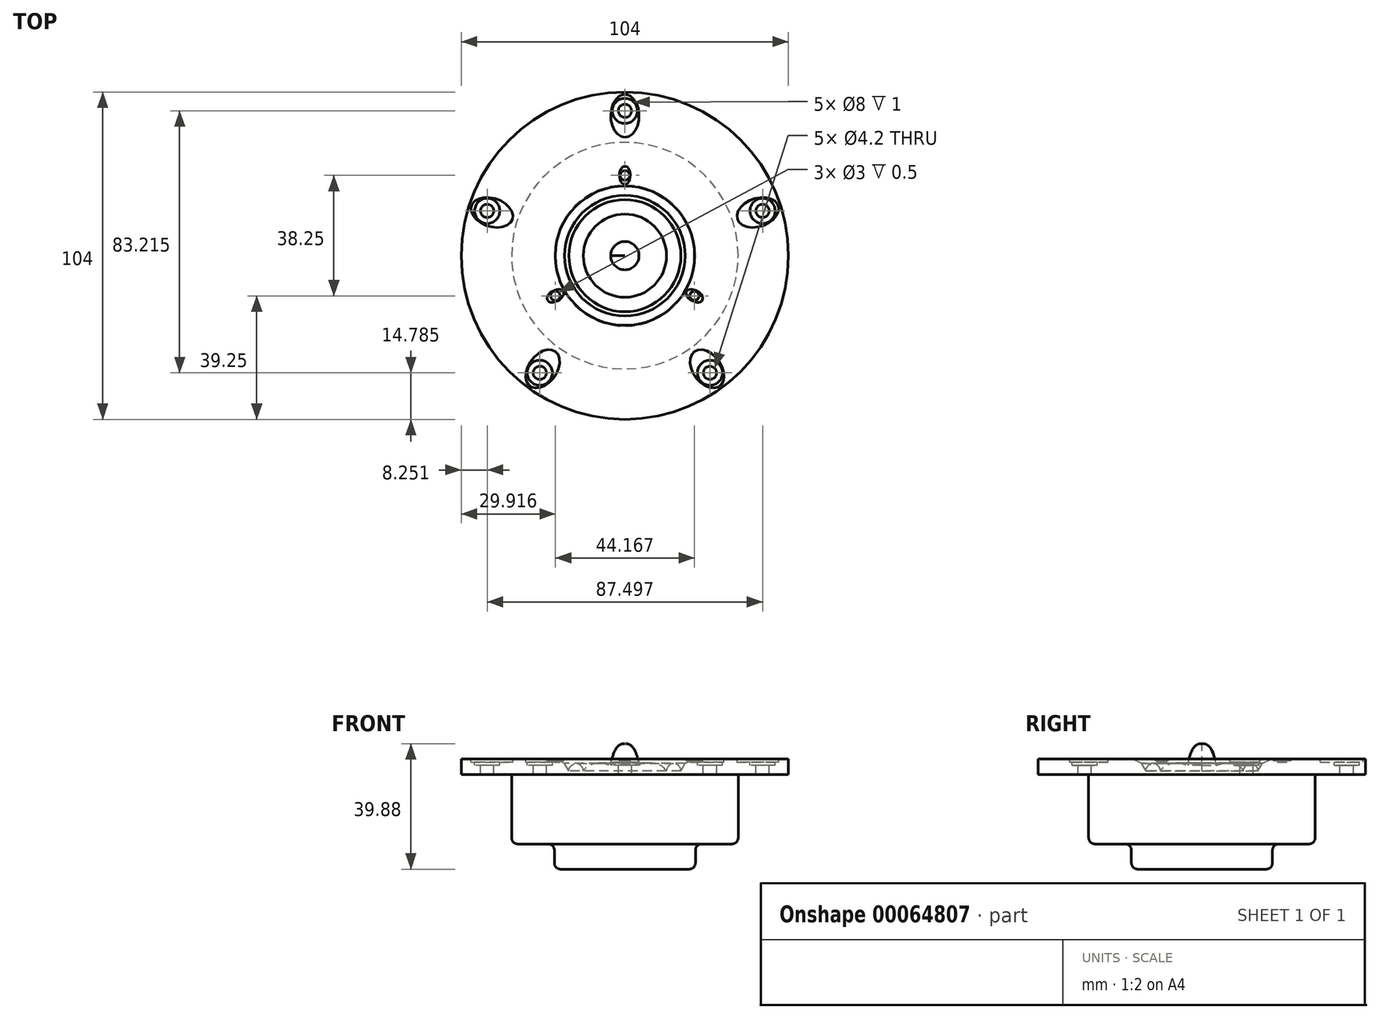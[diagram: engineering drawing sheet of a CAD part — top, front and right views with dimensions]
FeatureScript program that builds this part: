
annotation { "Feature Type Name" : "Feature", "Feature Type Description" : "" }
export const myFeature = defineFeature(function(context is Context, id is Id, definition is map)
    precondition{}
    {
        {
            var Q0;
            Q0=qCreatedBy(makeId("Front.planeOp"),FACE);
            var sketch = newSketch(context, id + "F7", { "sketchPlane" : qUnion([Q0])});
            skLineSegment(sketch, "E0", {"start": v(-52, 16.61) * mm, "end": v(-22.14, 16.61) * mm});
            skLineSegment(sketch, "E1", {"start": v(-52, 16.61) * mm, "end": v(-52, 11.61) * mm});
            skLineSegment(sketch, "E2", {"start": v(-52, 11.61) * mm, "end": v(-36, 11.61) * mm});
            skLineSegment(sketch, "E3", {"start": v(-36, 11.61) * mm, "end": v(-36, -8.39) * mm});
            skLineSegment(sketch, "E4", {"start": v(-20.42, -18.39) * mm, "end": v(0, -18.39) * mm});
            skLineSegment(sketch, "E5", {"start": v(0, 18.61) * mm, "end": v(0, -18.39) * mm});
            skArc(sketch, "E6", {"start": v(-13.22, 12.8) * mm, "mid": v(-15.52, 15.1) * mm, "end": v(-17.82, 12.8) * mm});
            skLineSegment(sketch, "E7", {"start": v(-17.82, 12.8) * mm, "end": v(-19.15, 15.25) * mm});
            skPoint(sketch, "E8.start.orphan", {"position": v(-13.22, 16.61) * mm});
            skFitSpline(sketch, "E9", {"points": [v(-13.22, 12.8) * mm, v(-4.5, 14.54) * mm], "startDerivative": vector(3.61, 6.94) * mm, "endDerivative": vector(10.05, -4.73) * mm});
            skFitSpline(sketch, "E10", {"points": [v(-4.5, 14.54) * mm, v(-3.15, 19.3) * mm, v(0, 21.48) * mm], "startDerivative": vector(0.28, 7.18) * mm, "endDerivative": vector(10.4, -0.77) * mm});
            skLineSegment(sketch, "E11", {"start": v(0, 21.48) * mm, "end": v(0, 18.61) * mm});
            skLineSegment(sketch, "E12", {"start": v(-22.14, 16.61) * mm, "end": v(-19.15, 15.25) * mm});
            skLineSegment(sketch, "E13", {"start": v(-22.42, -16.39) * mm, "end": v(-22.42, -12.39) * mm});
            skLineSegment(sketch, "E14", {"start": v(-24.42, -10.39) * mm, "end": v(-34, -10.39) * mm});
            skPoint(sketch, "E15.visualSharp", {"position": v(-22.42, -10.39) * mm});
            skArc(sketch, "E15.filletArc", {"start": v(-22.42, -12.39) * mm, "mid": v(-23, -10.97) * mm, "end": v(-24.42, -10.39) * mm});
            skPoint(sketch, "E16.orphan", {"position": v(-36, -18.39) * mm});
            skPoint(sketch, "E17.visualSharp", {"position": v(-22.42, -18.39) * mm});
            skArc(sketch, "E17.filletArc", {"start": v(-22.42, -16.39) * mm, "mid": v(-21.83, -17.8) * mm, "end": v(-20.42, -18.39) * mm});
            skPoint(sketch, "E18.visualSharp", {"position": v(-36, -10.39) * mm});
            skArc(sketch, "E18.filletArc", {"start": v(-36, -8.39) * mm, "mid": v(-35.41, -9.8) * mm, "end": v(-34, -10.39) * mm});
            skSolve(sketch);
        }
        {
            var Q0;
            Q0 = qSketchRegion(id + "F7", true);
            var Q1;
            Q1=sQuery(id+"F7.wireOp",EDGE,"E5");
            revolve(context, id + "F8", {"entities" : qUnion([Q0]), "axis" : qUnion([Q1]), "revolveType" : RevolveType.FULL});
        }
        {
            var Q0;
            Q0=makeQuery(id+"F8.opRevolve","SWEPT_FACE",FACE,{"disambiguationData":[OSD([sQuery(id+"F7.wireOp",EDGE,"E0")])]});
            var sketch = newSketch(context, id + "F0", { "sketchPlane" : qUnion([Q0])});
            skCircle(sketch, "E19", {"center": v(0, 0) * mm, "radius": 46 * mm});
            skPoint(sketch, "E20", {"position": v(0, 46) * mm});
            skCircle(sketch, "E21", {"center": v(0, 46) * mm, "radius": 2.1 * mm});
            skCircle(sketch, "E22", {"center": v(0, 46) * mm, "radius": 4 * mm});
            skEllipse(sketch, "E23", {"center": v(0, 44.42) * mm, "majorRadius": 6.82 * mm, "minorRadius": 4.5 * mm, "majorAxis": v(0, -1)});
            skCircle(sketch, "E24.1.0", {"center": v(-43.75, 14.21) * mm, "radius": 2.1 * mm});
            skCircle(sketch, "E24.1.1", {"center": v(-43.75, 14.21) * mm, "radius": 4 * mm});
            skEllipse(sketch, "E24.1.2", {"center": v(-42.24, 13.73) * mm, "majorRadius": 6.82 * mm, "minorRadius": 4.5 * mm, "majorAxis": v(0.95, -0.3)});
            skCircle(sketch, "E24.2.0", {"center": v(-27.04, -37.21) * mm, "radius": 2.1 * mm});
            skCircle(sketch, "E24.2.1", {"center": v(-27.04, -37.21) * mm, "radius": 4 * mm});
            skEllipse(sketch, "E24.2.2", {"center": v(-26.1, -35.93) * mm, "majorRadius": 6.82 * mm, "minorRadius": 4.5 * mm, "majorAxis": v(0.59, 0.8)});
            skCircle(sketch, "E24.3.0", {"center": v(27.04, -37.21) * mm, "radius": 2.1 * mm});
            skCircle(sketch, "E24.3.1", {"center": v(27.04, -37.21) * mm, "radius": 4 * mm});
            skEllipse(sketch, "E24.3.2", {"center": v(26.1, -35.93) * mm, "majorRadius": 6.82 * mm, "minorRadius": 4.5 * mm, "majorAxis": v(-0.59, 0.8)});
            skCircle(sketch, "E24.4.0", {"center": v(43.75, 14.21) * mm, "radius": 2.1 * mm});
            skCircle(sketch, "E24.4.1", {"center": v(43.75, 14.21) * mm, "radius": 4 * mm});
            skEllipse(sketch, "E24.4.2", {"center": v(42.24, 13.73) * mm, "majorRadius": 6.82 * mm, "minorRadius": 4.5 * mm, "majorAxis": v(-0.95, -0.3)});
            skCircle(sketch, "E25", {"center": v(0, 0) * mm, "radius": 25.5 * mm});
            skCircle(sketch, "E26", {"center": v(0, 25.5) * mm, "radius": 1.5 * mm});
            skPoint(sketch, "E27.center", {"position": v(-1.13, -3.98) * mm});
            skEllipse(sketch, "E28", {"center": v(0, 25.5) * mm, "majorRadius": 2.89 * mm, "minorRadius": 1.73 * mm, "majorAxis": v(0, -1)});
            skEllipse(sketch, "E29.1.0", {"center": v(-22.08, -12.75) * mm, "majorRadius": 2.89 * mm, "minorRadius": 1.73 * mm, "majorAxis": v(0.87, 0.5)});
            skCircle(sketch, "E29.1.1", {"center": v(-22.08, -12.75) * mm, "radius": 1.5 * mm});
            skEllipse(sketch, "E29.2.0", {"center": v(22.08, -12.75) * mm, "majorRadius": 2.89 * mm, "minorRadius": 1.73 * mm, "majorAxis": v(-0.87, 0.5)});
            skCircle(sketch, "E29.2.1", {"center": v(22.08, -12.75) * mm, "radius": 1.5 * mm});
            skSolve(sketch);
        }
        {
            var Q0;
            {var subQ0=sQuery(id+"F0.wireOp",EDGE,"E29.4.2");var subQ1=sQuery(id+"F0.wireOp",EDGE,"E29.1.1");var subQ2=makeQuery(id+"F0.imprint","INTERSECT",VERTEX,{"disambiguationData":[OD(0.0)],"derivedFrom":[subQ1,subQ0]});Q0=makeQuery(id+"F0.imprint","IMPRINT",FACE,{"disambiguationData":[TD([[makeQuery(id+"F0.imprint","IMPRINT",EDGE,{"disambiguationData":[TD([[subQ2,-1.0]])],"derivedFrom":subQ1}),1.0]])]});}
            var Q1;
            {var subQ0=sQuery(id+"F0.wireOp",EDGE,"E29.4.2");var subQ1=sQuery(id+"F0.wireOp",EDGE,"E29.1.1");var subQ2=makeQuery(id+"F0.imprint","INTERSECT",VERTEX,{"disambiguationData":[OD(0.0)],"derivedFrom":[subQ1,subQ0]});Q1=makeQuery(id+"F0.imprint","IMPRINT",FACE,{"disambiguationData":[TD([[makeQuery(id+"F0.imprint","IMPRINT",EDGE,{"disambiguationData":[TD([[subQ2,1.0]])],"derivedFrom":subQ1}),1.0]])]});}
            var Q2;
            {var subQ0=sQuery(id+"F0.wireOp",EDGE,"E29.4.2");var subQ1=sQuery(id+"F0.wireOp",EDGE,"E26");var subQ2=makeQuery(id+"F0.imprint","INTERSECT",VERTEX,{"disambiguationData":[OD(0.0)],"derivedFrom":[subQ1,subQ0]});Q2=makeQuery(id+"F0.imprint","IMPRINT",FACE,{"disambiguationData":[TD([[makeQuery(id+"F0.imprint","IMPRINT",EDGE,{"disambiguationData":[TD([[subQ2,-1.0]])],"derivedFrom":subQ1}),1.0]])]});}
            var Q3;
            {var subQ0=sQuery(id+"F0.wireOp",EDGE,"E29.4.2");var subQ1=sQuery(id+"F0.wireOp",EDGE,"E26");var subQ2=makeQuery(id+"F0.imprint","INTERSECT",VERTEX,{"disambiguationData":[OD(0.0)],"derivedFrom":[subQ1,subQ0]});Q3=makeQuery(id+"F0.imprint","IMPRINT",FACE,{"disambiguationData":[TD([[makeQuery(id+"F0.imprint","IMPRINT",EDGE,{"disambiguationData":[TD([[subQ2,1.0]])],"derivedFrom":subQ1}),1.0]])]});}
            var Q4;
            {var subQ0=sQuery(id+"F0.wireOp",EDGE,"E29.4.2");var subQ1=sQuery(id+"F0.wireOp",EDGE,"E29.4.1");var subQ2=makeQuery(id+"F0.imprint","INTERSECT",VERTEX,{"disambiguationData":[OD(0.0)],"derivedFrom":[subQ1,subQ0]});Q4=makeQuery(id+"F0.imprint","IMPRINT",FACE,{"disambiguationData":[TD([[makeQuery(id+"F0.imprint","IMPRINT",EDGE,{"disambiguationData":[TD([[subQ2,-1.0]])],"derivedFrom":subQ1}),1.0]])]});}
            var Q5;
            {var subQ0=sQuery(id+"F0.wireOp",EDGE,"E29.4.2");var subQ1=sQuery(id+"F0.wireOp",EDGE,"E29.4.1");var subQ2=makeQuery(id+"F0.imprint","INTERSECT",VERTEX,{"disambiguationData":[OD(0.0)],"derivedFrom":[subQ1,subQ0]});Q5=makeQuery(id+"F0.imprint","IMPRINT",FACE,{"disambiguationData":[TD([[makeQuery(id+"F0.imprint","IMPRINT",EDGE,{"disambiguationData":[TD([[subQ2,1.0]])],"derivedFrom":subQ1}),1.0]])]});}
            var Q6;
            {var subQ0=sQuery(id+"F0.wireOp",EDGE,"E29.4.2");var subQ1=sQuery(id+"F0.wireOp",EDGE,"E29.3.1");var subQ2=makeQuery(id+"F0.imprint","INTERSECT",VERTEX,{"disambiguationData":[OD(0.0)],"derivedFrom":[subQ1,subQ0]});Q6=makeQuery(id+"F0.imprint","IMPRINT",FACE,{"disambiguationData":[TD([[makeQuery(id+"F0.imprint","IMPRINT",EDGE,{"disambiguationData":[TD([[subQ2,-1.0]])],"derivedFrom":subQ1}),1.0]])]});}
            var Q7;
            {var subQ0=sQuery(id+"F0.wireOp",EDGE,"E29.4.2");var subQ1=sQuery(id+"F0.wireOp",EDGE,"E29.3.1");var subQ2=makeQuery(id+"F0.imprint","INTERSECT",VERTEX,{"disambiguationData":[OD(0.0)],"derivedFrom":[subQ1,subQ0]});Q7=makeQuery(id+"F0.imprint","IMPRINT",FACE,{"disambiguationData":[TD([[makeQuery(id+"F0.imprint","IMPRINT",EDGE,{"disambiguationData":[TD([[subQ2,1.0]])],"derivedFrom":subQ1}),1.0]])]});}
            var Q8;
            {var subQ0=sQuery(id+"F0.wireOp",EDGE,"E29.4.2");var subQ1=sQuery(id+"F0.wireOp",EDGE,"E29.2.1");var subQ2=makeQuery(id+"F0.imprint","INTERSECT",VERTEX,{"disambiguationData":[OD(0.0)],"derivedFrom":[subQ1,subQ0]});Q8=makeQuery(id+"F0.imprint","IMPRINT",FACE,{"disambiguationData":[TD([[makeQuery(id+"F0.imprint","IMPRINT",EDGE,{"disambiguationData":[TD([[subQ2,-1.0]])],"derivedFrom":subQ1}),1.0]])]});}
            var Q9;
            {var subQ0=sQuery(id+"F0.wireOp",EDGE,"E29.4.2");var subQ1=sQuery(id+"F0.wireOp",EDGE,"E29.2.1");var subQ2=makeQuery(id+"F0.imprint","INTERSECT",VERTEX,{"disambiguationData":[OD(0.0)],"derivedFrom":[subQ1,subQ0]});Q9=makeQuery(id+"F0.imprint","IMPRINT",FACE,{"disambiguationData":[TD([[makeQuery(id+"F0.imprint","IMPRINT",EDGE,{"disambiguationData":[TD([[subQ2,1.0]])],"derivedFrom":subQ1}),1.0]])]});}
            extrude(context, id + "F1", {"entities" : qUnion([Q0, Q1, Q2, Q3, Q4, Q5, Q6, Q7, Q8, Q9]), "operationType" : NewBodyOperationType.REMOVE, "oppositeDirection" : true, "depth" : 1 * mm});
        }
        {
            var Q0;
            {var subQ0=sQuery(id+"F0.wireOp",EDGE,"E29.4.2");var subQ1=sQuery(id+"F0.wireOp",EDGE,"E29.1.0");var subQ2=makeQuery(id+"F0.imprint","INTERSECT",VERTEX,{"disambiguationData":[OD(0.0)],"derivedFrom":[subQ1,subQ0]});Q0=makeQuery(id+"F0.imprint","IMPRINT",FACE,{"disambiguationData":[TD([[makeQuery(id+"F0.imprint","IMPRINT",EDGE,{"disambiguationData":[TD([[subQ2,-1.0]])],"derivedFrom":subQ1}),1.0]])]});}
            var Q1;
            {var subQ0=sQuery(id+"F0.wireOp",EDGE,"E29.4.2");var subQ1=sQuery(id+"F0.wireOp",EDGE,"E29.1.0");var subQ2=makeQuery(id+"F0.imprint","INTERSECT",VERTEX,{"disambiguationData":[OD(0.0)],"derivedFrom":[subQ1,subQ0]});Q1=makeQuery(id+"F0.imprint","IMPRINT",FACE,{"disambiguationData":[TD([[makeQuery(id+"F0.imprint","IMPRINT",EDGE,{"disambiguationData":[TD([[subQ2,1.0]])],"derivedFrom":subQ1}),1.0]])]});}
            var Q2;
            {var subQ0=sQuery(id+"F0.wireOp",EDGE,"E29.4.2");var subQ1=sQuery(id+"F0.wireOp",EDGE,"E26");var subQ2=makeQuery(id+"F0.imprint","INTERSECT",VERTEX,{"disambiguationData":[OD(0.0)],"derivedFrom":[subQ1,subQ0]});Q2=makeQuery(id+"F0.imprint","IMPRINT",FACE,{"disambiguationData":[TD([[makeQuery(id+"F0.imprint","IMPRINT",EDGE,{"disambiguationData":[TD([[subQ2,-1.0]])],"derivedFrom":subQ1}),-1.0]])]});}
            var Q3;
            {var subQ0=sQuery(id+"F0.wireOp",EDGE,"E29.4.2");var subQ1=sQuery(id+"F0.wireOp",EDGE,"E26");var subQ2=makeQuery(id+"F0.imprint","INTERSECT",VERTEX,{"disambiguationData":[OD(0.0)],"derivedFrom":[subQ1,subQ0]});Q3=makeQuery(id+"F0.imprint","IMPRINT",FACE,{"disambiguationData":[TD([[makeQuery(id+"F0.imprint","IMPRINT",EDGE,{"disambiguationData":[TD([[subQ2,1.0]])],"derivedFrom":subQ1}),-1.0]])]});}
            var Q4;
            {var subQ0=sQuery(id+"F0.wireOp",EDGE,"E29.4.2");var subQ1=sQuery(id+"F0.wireOp",EDGE,"E29.4.0");var subQ2=makeQuery(id+"F0.imprint","INTERSECT",VERTEX,{"disambiguationData":[OD(0.0)],"derivedFrom":[subQ1,subQ0]});Q4=makeQuery(id+"F0.imprint","IMPRINT",FACE,{"disambiguationData":[TD([[makeQuery(id+"F0.imprint","IMPRINT",EDGE,{"disambiguationData":[TD([[subQ2,-1.0]])],"derivedFrom":subQ1}),1.0]])]});}
            var Q5;
            {var subQ0=sQuery(id+"F0.wireOp",EDGE,"E29.4.2");var subQ1=sQuery(id+"F0.wireOp",EDGE,"E29.4.0");var subQ2=makeQuery(id+"F0.imprint","INTERSECT",VERTEX,{"disambiguationData":[OD(0.0)],"derivedFrom":[subQ1,subQ0]});Q5=makeQuery(id+"F0.imprint","IMPRINT",FACE,{"disambiguationData":[TD([[makeQuery(id+"F0.imprint","IMPRINT",EDGE,{"disambiguationData":[TD([[subQ2,1.0]])],"derivedFrom":subQ1}),1.0]])]});}
            var Q6;
            {var subQ0=sQuery(id+"F0.wireOp",EDGE,"E29.4.2");var subQ1=sQuery(id+"F0.wireOp",EDGE,"E29.3.0");var subQ2=makeQuery(id+"F0.imprint","INTERSECT",VERTEX,{"disambiguationData":[OD(0.0)],"derivedFrom":[subQ1,subQ0]});Q6=makeQuery(id+"F0.imprint","IMPRINT",FACE,{"disambiguationData":[TD([[makeQuery(id+"F0.imprint","IMPRINT",EDGE,{"disambiguationData":[TD([[subQ2,-1.0]])],"derivedFrom":subQ1}),1.0]])]});}
            var Q7;
            {var subQ0=sQuery(id+"F0.wireOp",EDGE,"E29.4.2");var subQ1=sQuery(id+"F0.wireOp",EDGE,"E29.3.0");var subQ2=makeQuery(id+"F0.imprint","INTERSECT",VERTEX,{"disambiguationData":[OD(0.0)],"derivedFrom":[subQ1,subQ0]});Q7=makeQuery(id+"F0.imprint","IMPRINT",FACE,{"disambiguationData":[TD([[makeQuery(id+"F0.imprint","IMPRINT",EDGE,{"disambiguationData":[TD([[subQ2,1.0]])],"derivedFrom":subQ1}),1.0]])]});}
            var Q8;
            {var subQ0=sQuery(id+"F0.wireOp",EDGE,"E29.4.2");var subQ1=sQuery(id+"F0.wireOp",EDGE,"E29.2.0");var subQ2=makeQuery(id+"F0.imprint","INTERSECT",VERTEX,{"disambiguationData":[OD(0.0)],"derivedFrom":[subQ1,subQ0]});Q8=makeQuery(id+"F0.imprint","IMPRINT",FACE,{"disambiguationData":[TD([[makeQuery(id+"F0.imprint","IMPRINT",EDGE,{"disambiguationData":[TD([[subQ2,-1.0]])],"derivedFrom":subQ1}),1.0]])]});}
            var Q9;
            {var subQ0=sQuery(id+"F0.wireOp",EDGE,"E29.4.2");var subQ1=sQuery(id+"F0.wireOp",EDGE,"E29.2.0");var subQ2=makeQuery(id+"F0.imprint","INTERSECT",VERTEX,{"disambiguationData":[OD(0.0)],"derivedFrom":[subQ1,subQ0]});Q9=makeQuery(id+"F0.imprint","IMPRINT",FACE,{"disambiguationData":[TD([[makeQuery(id+"F0.imprint","IMPRINT",EDGE,{"disambiguationData":[TD([[subQ2,1.0]])],"derivedFrom":subQ1}),1.0]])]});}
            extrude(context, id + "F2", {"entities" : qUnion([Q0, Q1, Q2, Q3, Q4, Q5, Q6, Q7, Q8, Q9]), "operationType" : NewBodyOperationType.REMOVE, "oppositeDirection" : true, "depth" : 0.5 * mm});
        }
        {
            var Q0;
            {var subQ0=sQuery(id+"F0.wireOp",EDGE,"E19");var subQ1=sQuery(id+"F0.wireOp",EDGE,"E24.1.0");var subQ2=makeQuery(id+"F0.imprint","INTERSECT",VERTEX,{"disambiguationData":[OD(0.0)],"derivedFrom":[subQ1,subQ0]});Q0=makeQuery(id+"F0.imprint","IMPRINT",FACE,{"disambiguationData":[TD([[makeQuery(id+"F0.imprint","IMPRINT",EDGE,{"disambiguationData":[TD([[subQ2,-1.0]])],"derivedFrom":subQ1}),1.0]])]});}
            var Q1;
            {var subQ0=sQuery(id+"F0.wireOp",EDGE,"E19");var subQ1=sQuery(id+"F0.wireOp",EDGE,"E24.1.0");var subQ2=makeQuery(id+"F0.imprint","INTERSECT",VERTEX,{"disambiguationData":[OD(0.0)],"derivedFrom":[subQ1,subQ0]});Q1=makeQuery(id+"F0.imprint","IMPRINT",FACE,{"disambiguationData":[TD([[makeQuery(id+"F0.imprint","IMPRINT",EDGE,{"disambiguationData":[TD([[subQ2,1.0]])],"derivedFrom":subQ1}),1.0]])]});}
            var Q2;
            {var subQ0=sQuery(id+"F0.wireOp",EDGE,"E19");var subQ1=sQuery(id+"F0.wireOp",EDGE,"E21");var subQ2=makeQuery(id+"F0.imprint","INTERSECT",VERTEX,{"disambiguationData":[OD(0.0)],"derivedFrom":[subQ1,subQ0]});Q2=makeQuery(id+"F0.imprint","IMPRINT",FACE,{"disambiguationData":[TD([[makeQuery(id+"F0.imprint","IMPRINT",EDGE,{"disambiguationData":[TD([[subQ2,-1.0]])],"derivedFrom":subQ1}),1.0]])]});}
            var Q3;
            {var subQ0=sQuery(id+"F0.wireOp",EDGE,"E19");var subQ1=sQuery(id+"F0.wireOp",EDGE,"E21");var subQ2=makeQuery(id+"F0.imprint","INTERSECT",VERTEX,{"disambiguationData":[OD(0.0)],"derivedFrom":[subQ1,subQ0]});Q3=makeQuery(id+"F0.imprint","IMPRINT",FACE,{"disambiguationData":[TD([[makeQuery(id+"F0.imprint","IMPRINT",EDGE,{"disambiguationData":[TD([[subQ2,1.0]])],"derivedFrom":subQ1}),1.0]])]});}
            var Q4;
            {var subQ0=sQuery(id+"F0.wireOp",EDGE,"E19");var subQ1=sQuery(id+"F0.wireOp",EDGE,"E24.4.0");var subQ2=makeQuery(id+"F0.imprint","INTERSECT",VERTEX,{"disambiguationData":[OD(0.0)],"derivedFrom":[subQ1,subQ0]});Q4=makeQuery(id+"F0.imprint","IMPRINT",FACE,{"disambiguationData":[TD([[makeQuery(id+"F0.imprint","IMPRINT",EDGE,{"disambiguationData":[TD([[subQ2,-1.0]])],"derivedFrom":subQ1}),1.0]])]});}
            var Q5;
            {var subQ0=sQuery(id+"F0.wireOp",EDGE,"E19");var subQ1=sQuery(id+"F0.wireOp",EDGE,"E24.4.0");var subQ2=makeQuery(id+"F0.imprint","INTERSECT",VERTEX,{"disambiguationData":[OD(0.0)],"derivedFrom":[subQ1,subQ0]});Q5=makeQuery(id+"F0.imprint","IMPRINT",FACE,{"disambiguationData":[TD([[makeQuery(id+"F0.imprint","IMPRINT",EDGE,{"disambiguationData":[TD([[subQ2,1.0]])],"derivedFrom":subQ1}),1.0]])]});}
            var Q6;
            {var subQ0=sQuery(id+"F0.wireOp",EDGE,"E19");var subQ1=sQuery(id+"F0.wireOp",EDGE,"E24.3.0");var subQ2=makeQuery(id+"F0.imprint","INTERSECT",VERTEX,{"disambiguationData":[OD(0.0)],"derivedFrom":[subQ1,subQ0]});Q6=makeQuery(id+"F0.imprint","IMPRINT",FACE,{"disambiguationData":[TD([[makeQuery(id+"F0.imprint","IMPRINT",EDGE,{"disambiguationData":[TD([[subQ2,-1.0]])],"derivedFrom":subQ1}),1.0]])]});}
            var Q7;
            {var subQ0=sQuery(id+"F0.wireOp",EDGE,"E19");var subQ1=sQuery(id+"F0.wireOp",EDGE,"E24.3.0");var subQ2=makeQuery(id+"F0.imprint","INTERSECT",VERTEX,{"disambiguationData":[OD(0.0)],"derivedFrom":[subQ1,subQ0]});Q7=makeQuery(id+"F0.imprint","IMPRINT",FACE,{"disambiguationData":[TD([[makeQuery(id+"F0.imprint","IMPRINT",EDGE,{"disambiguationData":[TD([[subQ2,1.0]])],"derivedFrom":subQ1}),1.0]])]});}
            var Q8;
            {var subQ0=sQuery(id+"F0.wireOp",EDGE,"E19");var subQ1=sQuery(id+"F0.wireOp",EDGE,"E24.2.0");var subQ2=makeQuery(id+"F0.imprint","INTERSECT",VERTEX,{"disambiguationData":[OD(0.0)],"derivedFrom":[subQ1,subQ0]});Q8=makeQuery(id+"F0.imprint","IMPRINT",FACE,{"disambiguationData":[TD([[makeQuery(id+"F0.imprint","IMPRINT",EDGE,{"disambiguationData":[TD([[subQ2,-1.0]])],"derivedFrom":subQ1}),1.0]])]});}
            var Q9;
            {var subQ0=sQuery(id+"F0.wireOp",EDGE,"E19");var subQ1=sQuery(id+"F0.wireOp",EDGE,"E24.2.0");var subQ2=makeQuery(id+"F0.imprint","INTERSECT",VERTEX,{"disambiguationData":[OD(0.0)],"derivedFrom":[subQ1,subQ0]});Q9=makeQuery(id+"F0.imprint","IMPRINT",FACE,{"disambiguationData":[TD([[makeQuery(id+"F0.imprint","IMPRINT",EDGE,{"disambiguationData":[TD([[subQ2,1.0]])],"derivedFrom":subQ1}),1.0]])]});}
            extrude(context, id + "F3", {"entities" : qUnion([Q0, Q1, Q2, Q3, Q4, Q5, Q6, Q7, Q8, Q9]), "operationType" : NewBodyOperationType.REMOVE, "endBound" : BoundingType.THROUGH_ALL, "oppositeDirection" : true, "depth" : 25 * mm});
        }
        {
            var Q0;
            {var subQ3=sQuery(id+"F0.wireOp",EDGE,"E19");var subQ9=sQuery(id+"F0.wireOp",EDGE,"E24.1.0");var subQ10=makeQuery(id+"F0.imprint","INTERSECT",VERTEX,{"disambiguationData":[OD(0.0)],"derivedFrom":[subQ9,subQ3]});Q0=makeQuery(id+"F0.imprint","IMPRINT",FACE,{"disambiguationData":[TD([[makeQuery(id+"F0.imprint","IMPRINT",EDGE,{"disambiguationData":[TD([[subQ10,-1.0]])],"derivedFrom":subQ9}),-1.0]])]});}
            var Q1;
            {var subQ0=sQuery(id+"F0.wireOp",EDGE,"E19");var subQ1=sQuery(id+"F0.wireOp",EDGE,"E24.1.0");var subQ2=makeQuery(id+"F0.imprint","INTERSECT",VERTEX,{"disambiguationData":[OD(0.0)],"derivedFrom":[subQ1,subQ0]});Q1=makeQuery(id+"F0.imprint","IMPRINT",FACE,{"disambiguationData":[TD([[makeQuery(id+"F0.imprint","IMPRINT",EDGE,{"disambiguationData":[TD([[subQ2,1.0]])],"derivedFrom":subQ1}),-1.0]])]});}
            var Q2;
            {var subQ0=sQuery(id+"F0.wireOp",EDGE,"E19");var subQ1=sQuery(id+"F0.wireOp",EDGE,"E21");var subQ2=makeQuery(id+"F0.imprint","INTERSECT",VERTEX,{"disambiguationData":[OD(0.0)],"derivedFrom":[subQ1,subQ0]});Q2=makeQuery(id+"F0.imprint","IMPRINT",FACE,{"disambiguationData":[TD([[makeQuery(id+"F0.imprint","IMPRINT",EDGE,{"disambiguationData":[TD([[subQ2,1.0]])],"derivedFrom":subQ1}),-1.0]])]});}
            var Q3;
            {var subQ3=sQuery(id+"F0.wireOp",EDGE,"E19");var subQ5=sQuery(id+"F0.wireOp",EDGE,"E21");var subQ10=makeQuery(id+"F0.imprint","INTERSECT",VERTEX,{"disambiguationData":[OD(0.0)],"derivedFrom":[subQ5,subQ3]});Q3=makeQuery(id+"F0.imprint","IMPRINT",FACE,{"disambiguationData":[TD([[makeQuery(id+"F0.imprint","IMPRINT",EDGE,{"disambiguationData":[TD([[subQ10,-1.0]])],"derivedFrom":subQ5}),-1.0]])]});}
            var Q4;
            {var subQ0=sQuery(id+"F0.wireOp",EDGE,"E19");var subQ1=sQuery(id+"F0.wireOp",EDGE,"E24.4.0");var subQ2=makeQuery(id+"F0.imprint","INTERSECT",VERTEX,{"disambiguationData":[OD(0.0)],"derivedFrom":[subQ1,subQ0]});Q4=makeQuery(id+"F0.imprint","IMPRINT",FACE,{"disambiguationData":[TD([[makeQuery(id+"F0.imprint","IMPRINT",EDGE,{"disambiguationData":[TD([[subQ2,1.0]])],"derivedFrom":subQ1}),-1.0]])]});}
            var Q5;
            {var subQ3=sQuery(id+"F0.wireOp",EDGE,"E19");var subQ5=sQuery(id+"F0.wireOp",EDGE,"E24.4.0");var subQ6=makeQuery(id+"F0.imprint","INTERSECT",VERTEX,{"disambiguationData":[OD(0.0)],"derivedFrom":[subQ5,subQ3]});Q5=makeQuery(id+"F0.imprint","IMPRINT",FACE,{"disambiguationData":[TD([[makeQuery(id+"F0.imprint","IMPRINT",EDGE,{"disambiguationData":[TD([[subQ6,-1.0]])],"derivedFrom":subQ5}),-1.0]])]});}
            var Q6;
            {var subQ0=sQuery(id+"F0.wireOp",EDGE,"E19");var subQ1=sQuery(id+"F0.wireOp",EDGE,"E24.3.0");var subQ2=makeQuery(id+"F0.imprint","INTERSECT",VERTEX,{"disambiguationData":[OD(0.0)],"derivedFrom":[subQ1,subQ0]});Q6=makeQuery(id+"F0.imprint","IMPRINT",FACE,{"disambiguationData":[TD([[makeQuery(id+"F0.imprint","IMPRINT",EDGE,{"disambiguationData":[TD([[subQ2,1.0]])],"derivedFrom":subQ1}),-1.0]])]});}
            var Q7;
            {var subQ3=sQuery(id+"F0.wireOp",EDGE,"E19");var subQ9=sQuery(id+"F0.wireOp",EDGE,"E24.3.0");var subQ10=makeQuery(id+"F0.imprint","INTERSECT",VERTEX,{"disambiguationData":[OD(0.0)],"derivedFrom":[subQ9,subQ3]});Q7=makeQuery(id+"F0.imprint","IMPRINT",FACE,{"disambiguationData":[TD([[makeQuery(id+"F0.imprint","IMPRINT",EDGE,{"disambiguationData":[TD([[subQ10,-1.0]])],"derivedFrom":subQ9}),-1.0]])]});}
            var Q8;
            {var subQ3=sQuery(id+"F0.wireOp",EDGE,"E19");var subQ5=sQuery(id+"F0.wireOp",EDGE,"E24.2.0");var subQ11=makeQuery(id+"F0.imprint","INTERSECT",VERTEX,{"disambiguationData":[OD(0.0)],"derivedFrom":[subQ5,subQ3]});Q8=makeQuery(id+"F0.imprint","IMPRINT",FACE,{"disambiguationData":[TD([[makeQuery(id+"F0.imprint","IMPRINT",EDGE,{"disambiguationData":[TD([[subQ11,-1.0]])],"derivedFrom":subQ5}),-1.0]])]});}
            var Q9;
            {var subQ0=sQuery(id+"F0.wireOp",EDGE,"E19");var subQ1=sQuery(id+"F0.wireOp",EDGE,"E24.2.0");var subQ2=makeQuery(id+"F0.imprint","INTERSECT",VERTEX,{"disambiguationData":[OD(0.0)],"derivedFrom":[subQ1,subQ0]});Q9=makeQuery(id+"F0.imprint","IMPRINT",FACE,{"disambiguationData":[TD([[makeQuery(id+"F0.imprint","IMPRINT",EDGE,{"disambiguationData":[TD([[subQ2,1.0]])],"derivedFrom":subQ1}),-1.0]])]});}
            extrude(context, id + "F4", {"entities" : qUnion([Q0, Q1, Q2, Q3, Q4, Q5, Q6, Q7, Q8, Q9]), "operationType" : NewBodyOperationType.REMOVE, "oppositeDirection" : true, "depth" : 2 * mm});
        }
        {
            var Q0;
            {var subQ0=sQuery(id+"F0.wireOp",EDGE,"E19");var subQ1=sQuery(id+"F0.wireOp",EDGE,"E22");var subQ2=makeQuery(id+"F0.imprint","INTERSECT",VERTEX,{"disambiguationData":[OD(0.0)],"derivedFrom":[subQ1,subQ0]});Q0=makeQuery(id+"F0.imprint","IMPRINT",FACE,{"disambiguationData":[TD([[makeQuery(id+"F0.imprint","IMPRINT",EDGE,{"disambiguationData":[TD([[subQ2,1.0]])],"derivedFrom":subQ1}),-1.0]])]});}
            var Q1;
            {var subQ0=sQuery(id+"F0.wireOp",EDGE,"E19");var subQ1=sQuery(id+"F0.wireOp",EDGE,"E22");var subQ2=makeQuery(id+"F0.imprint","INTERSECT",VERTEX,{"disambiguationData":[OD(0.0)],"derivedFrom":[subQ1,subQ0]});Q1=makeQuery(id+"F0.imprint","IMPRINT",FACE,{"disambiguationData":[TD([[makeQuery(id+"F0.imprint","IMPRINT",EDGE,{"disambiguationData":[TD([[subQ2,-1.0]])],"derivedFrom":subQ1}),-1.0]])]});}
            var Q2;
            {var subQ0=sQuery(id+"F0.wireOp",EDGE,"E19");var subQ1=sQuery(id+"F0.wireOp",EDGE,"E24.1.1");var subQ2=makeQuery(id+"F0.imprint","INTERSECT",VERTEX,{"disambiguationData":[OD(0.0)],"derivedFrom":[subQ1,subQ0]});Q2=makeQuery(id+"F0.imprint","IMPRINT",FACE,{"disambiguationData":[TD([[makeQuery(id+"F0.imprint","IMPRINT",EDGE,{"disambiguationData":[TD([[subQ2,-1.0]])],"derivedFrom":subQ1}),-1.0]])]});}
            var Q3;
            {var subQ0=sQuery(id+"F0.wireOp",EDGE,"E19");var subQ1=sQuery(id+"F0.wireOp",EDGE,"E24.1.1");var subQ2=makeQuery(id+"F0.imprint","INTERSECT",VERTEX,{"disambiguationData":[OD(0.0)],"derivedFrom":[subQ1,subQ0]});Q3=makeQuery(id+"F0.imprint","IMPRINT",FACE,{"disambiguationData":[TD([[makeQuery(id+"F0.imprint","IMPRINT",EDGE,{"disambiguationData":[TD([[subQ2,1.0]])],"derivedFrom":subQ1}),-1.0]])]});}
            var Q4;
            {var subQ0=sQuery(id+"F0.wireOp",EDGE,"E19");var subQ1=sQuery(id+"F0.wireOp",EDGE,"E24.2.1");var subQ2=makeQuery(id+"F0.imprint","INTERSECT",VERTEX,{"disambiguationData":[OD(0.0)],"derivedFrom":[subQ1,subQ0]});Q4=makeQuery(id+"F0.imprint","IMPRINT",FACE,{"disambiguationData":[TD([[makeQuery(id+"F0.imprint","IMPRINT",EDGE,{"disambiguationData":[TD([[subQ2,-1.0]])],"derivedFrom":subQ1}),-1.0]])]});}
            var Q5;
            {var subQ0=sQuery(id+"F0.wireOp",EDGE,"E19");var subQ1=sQuery(id+"F0.wireOp",EDGE,"E24.2.1");var subQ2=makeQuery(id+"F0.imprint","INTERSECT",VERTEX,{"disambiguationData":[OD(0.0)],"derivedFrom":[subQ1,subQ0]});Q5=makeQuery(id+"F0.imprint","IMPRINT",FACE,{"disambiguationData":[TD([[makeQuery(id+"F0.imprint","IMPRINT",EDGE,{"disambiguationData":[TD([[subQ2,1.0]])],"derivedFrom":subQ1}),-1.0]])]});}
            var Q6;
            {var subQ0=sQuery(id+"F0.wireOp",EDGE,"E19");var subQ1=sQuery(id+"F0.wireOp",EDGE,"E24.3.1");var subQ2=makeQuery(id+"F0.imprint","INTERSECT",VERTEX,{"disambiguationData":[OD(0.0)],"derivedFrom":[subQ1,subQ0]});Q6=makeQuery(id+"F0.imprint","IMPRINT",FACE,{"disambiguationData":[TD([[makeQuery(id+"F0.imprint","IMPRINT",EDGE,{"disambiguationData":[TD([[subQ2,-1.0]])],"derivedFrom":subQ1}),-1.0]])]});}
            var Q7;
            {var subQ0=sQuery(id+"F0.wireOp",EDGE,"E19");var subQ1=sQuery(id+"F0.wireOp",EDGE,"E24.3.1");var subQ2=makeQuery(id+"F0.imprint","INTERSECT",VERTEX,{"disambiguationData":[OD(0.0)],"derivedFrom":[subQ1,subQ0]});Q7=makeQuery(id+"F0.imprint","IMPRINT",FACE,{"disambiguationData":[TD([[makeQuery(id+"F0.imprint","IMPRINT",EDGE,{"disambiguationData":[TD([[subQ2,1.0]])],"derivedFrom":subQ1}),-1.0]])]});}
            var Q8;
            {var subQ0=sQuery(id+"F0.wireOp",EDGE,"E19");var subQ1=sQuery(id+"F0.wireOp",EDGE,"E24.4.1");var subQ2=makeQuery(id+"F0.imprint","INTERSECT",VERTEX,{"disambiguationData":[OD(0.0)],"derivedFrom":[subQ1,subQ0]});Q8=makeQuery(id+"F0.imprint","IMPRINT",FACE,{"disambiguationData":[TD([[makeQuery(id+"F0.imprint","IMPRINT",EDGE,{"disambiguationData":[TD([[subQ2,-1.0]])],"derivedFrom":subQ1}),-1.0]])]});}
            var Q9;
            {var subQ0=sQuery(id+"F0.wireOp",EDGE,"E19");var subQ1=sQuery(id+"F0.wireOp",EDGE,"E24.4.1");var subQ2=makeQuery(id+"F0.imprint","INTERSECT",VERTEX,{"disambiguationData":[OD(0.0)],"derivedFrom":[subQ1,subQ0]});Q9=makeQuery(id+"F0.imprint","IMPRINT",FACE,{"disambiguationData":[TD([[makeQuery(id+"F0.imprint","IMPRINT",EDGE,{"disambiguationData":[TD([[subQ2,1.0]])],"derivedFrom":subQ1}),-1.0]])]});}
            extrude(context, id + "F5", {"entities" : qUnion([Q0, Q1, Q2, Q3, Q4, Q5, Q6, Q7, Q8, Q9]), "operationType" : NewBodyOperationType.REMOVE, "oppositeDirection" : true, "depth" : 1 * mm});
        }
        {
            var Q0;
            Q0=makeQuery(id+"F1.boolean.opBoolean","COPY",FACE,{"derivedFrom":makeQuery(id+"F1.opExtrude","CAP_FACE",FACE,{"disambiguationData":[OSD([sQuery(id+"F0.wireOp",EDGE,"E29.2.1")])],"isStart":false})});
            var sketch = newSketch(context, id + "F9", { "sketchPlane" : qUnion([Q0])});
            skCircle(sketch, "E30", {"center": v(22.08, -12.75) * mm, "radius": 1.4 * mm});
            skSolve(sketch);
        }
        {
            var Q0;
            Q0 = qSketchRegion(id + "F9", true);
            extrude(context, id + "F10", {"entities" : qUnion([Q0]), "operationType" : NewBodyOperationType.ADD, "depth" : 1 * mm});
        }
    });
